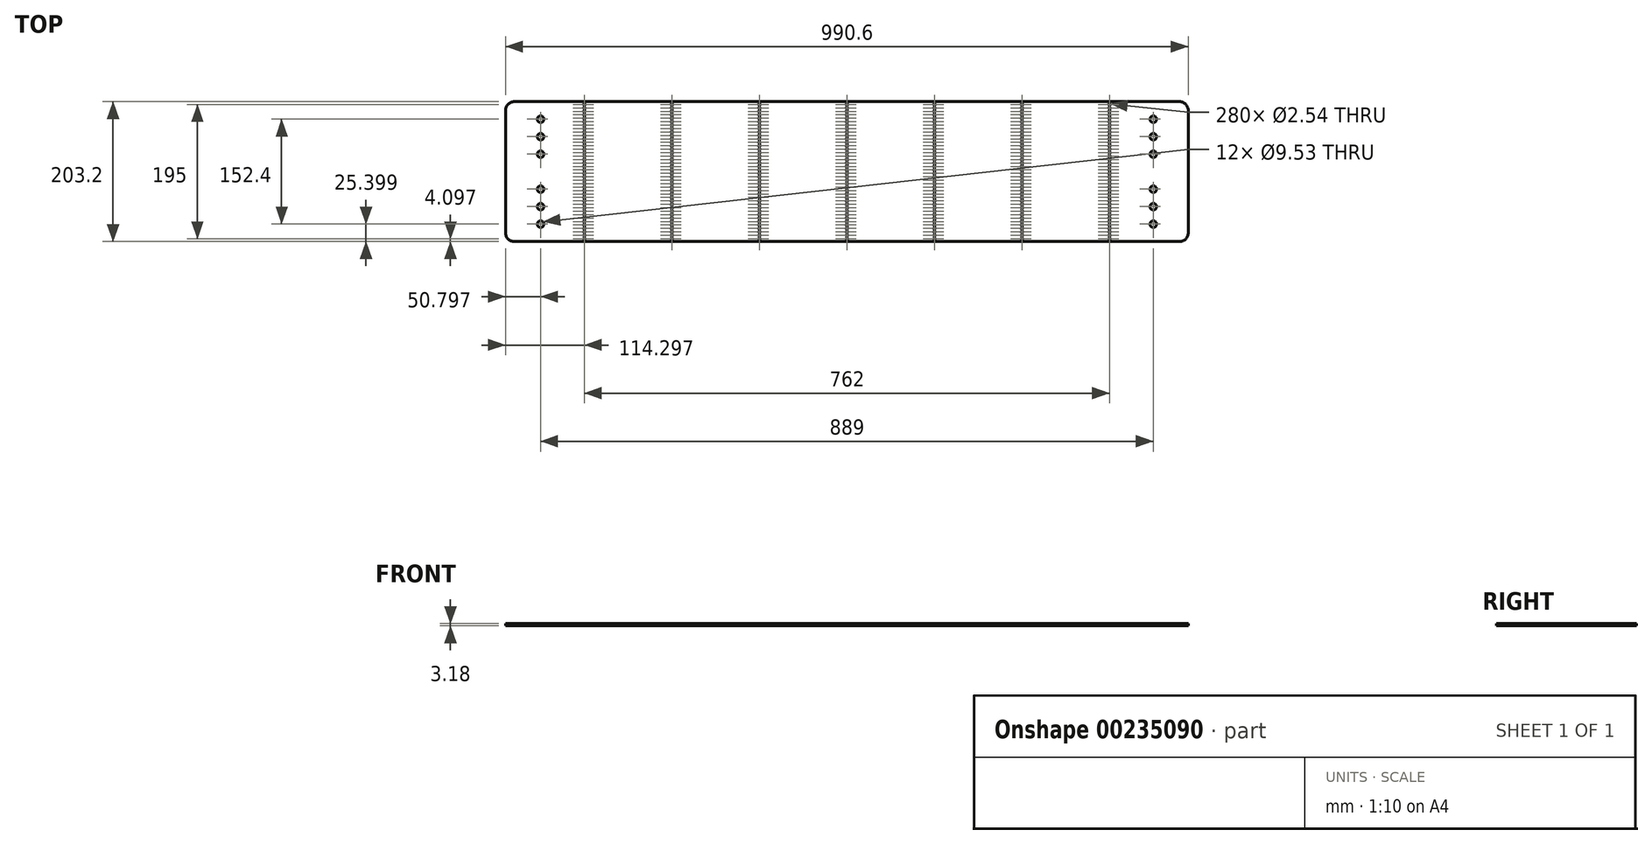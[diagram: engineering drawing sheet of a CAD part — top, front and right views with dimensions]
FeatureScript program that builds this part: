
annotation { "Feature Type Name" : "Feature", "Feature Type Description" : "" }
export const myFeature = defineFeature(function(context is Context, id is Id, definition is map)
    precondition{}
    {
        {
            var Q0;
            Q0=qCreatedBy(makeId("Top.planeOp"),FACE);
            var sketch = newSketch(context, id + "F0", { "sketchPlane" : qUnion([Q0])});
            skLineSegment(sketch, "E0.bottom", {"start": v(-546.73, 39.92) * mm, "end": v(418.47, 39.92) * mm});
            skLineSegment(sketch, "E0.top", {"start": v(-546.73, -163.28) * mm, "end": v(418.47, -163.28) * mm});
            skLineSegment(sketch, "E0.left", {"start": v(-559.43, 27.22) * mm, "end": v(-559.43, -150.58) * mm});
            skLineSegment(sketch, "E0.right", {"start": v(431.17, 27.22) * mm, "end": v(431.17, -150.58) * mm});
            skPoint(sketch, "E1.visualSharp", {"position": v(-559.43, 39.92) * mm});
            skArc(sketch, "E1.filletArc", {"start": v(-546.73, 39.92) * mm, "mid": v(-555.71, 36.2) * mm, "end": v(-559.43, 27.22) * mm});
            skPoint(sketch, "E2.visualSharp", {"position": v(-559.43, -163.28) * mm});
            skArc(sketch, "E2.filletArc", {"start": v(-559.43, -150.58) * mm, "mid": v(-555.71, -159.56) * mm, "end": v(-546.73, -163.28) * mm});
            skArc(sketch, "E3.filletArc", {"start": v(431.17, 27.22) * mm, "mid": v(427.45, 36.2) * mm, "end": v(418.47, 39.92) * mm});
            skArc(sketch, "E4.filletArc", {"start": v(418.47, -163.28) * mm, "mid": v(427.45, -159.56) * mm, "end": v(431.17, -150.58) * mm});
            skLineSegment(sketch, "E5", {"start": v(-559.43, -61.68) * mm, "end": v(-508.63, -61.68) * mm, "construction": true});
            skLineSegment(sketch, "E6", {"start": v(-508.63, 39.92) * mm, "end": v(-508.63, 14.52) * mm, "construction": true});
            skLineSegment(sketch, "E7", {"start": v(-508.63, -61.68) * mm, "end": v(-508.63, -87.08) * mm, "construction": true});
            skLineSegment(sketch, "E8", {"start": v(-508.63, -10.88) * mm, "end": v(-508.63, -36.28) * mm, "construction": true});
            skLineSegment(sketch, "E9", {"start": v(-508.63, -112.48) * mm, "end": v(-508.63, -137.88) * mm, "construction": true});
            skLineSegment(sketch, "E10", {"start": v(-508.63, 14.52) * mm, "end": v(-508.63, -10.88) * mm, "construction": true});
            skLineSegment(sketch, "E11", {"start": v(-508.63, -36.28) * mm, "end": v(-508.63, -61.68) * mm, "construction": true});
            skLineSegment(sketch, "E12", {"start": v(-508.63, -87.08) * mm, "end": v(-508.63, -112.48) * mm, "construction": true});
            skLineSegment(sketch, "E13", {"start": v(-508.63, -137.88) * mm, "end": v(-508.63, -163.28) * mm, "construction": true});
            skCircle(sketch, "E14", {"center": v(-508.63, 14.52) * mm, "radius": 4.76 * mm});
            skCircle(sketch, "E15", {"center": v(-508.63, -10.88) * mm, "radius": 4.76 * mm});
            skCircle(sketch, "E16", {"center": v(-508.63, -36.28) * mm, "radius": 4.76 * mm});
            skCircle(sketch, "E17", {"center": v(-508.63, -87.08) * mm, "radius": 4.76 * mm});
            skCircle(sketch, "E18", {"center": v(-508.63, -112.48) * mm, "radius": 4.76 * mm});
            skCircle(sketch, "E19", {"center": v(-508.63, -137.88) * mm, "radius": 4.76 * mm});
            skLineSegment(sketch, "E20", {"start": v(431.17, -61.68) * mm, "end": v(380.37, -61.68) * mm, "construction": true});
            skLineSegment(sketch, "E21", {"start": v(380.37, 39.92) * mm, "end": v(380.37, -163.28) * mm, "construction": true});
            skCircle(sketch, "E22", {"center": v(380.37, 14.52) * mm, "radius": 4.76 * mm});
            skCircle(sketch, "E23", {"center": v(380.37, -10.88) * mm, "radius": 4.76 * mm});
            skCircle(sketch, "E24", {"center": v(380.37, -36.28) * mm, "radius": 4.76 * mm});
            skCircle(sketch, "E25", {"center": v(380.37, -112.48) * mm, "radius": 4.76 * mm});
            skCircle(sketch, "E26", {"center": v(380.37, -87.08) * mm, "radius": 4.76 * mm});
            skCircle(sketch, "E27", {"center": v(380.37, -137.88) * mm, "radius": 4.76 * mm});
            skLineSegment(sketch, "E28", {"start": v(-508.63, -61.68) * mm, "end": v(-445.13, -61.68) * mm, "construction": true});
            skLineSegment(sketch, "E29", {"start": v(-445.13, 39.92) * mm, "end": v(-445.13, 35.82) * mm});
            skCircle(sketch, "E30", {"center": v(-445.13, 35.82) * mm, "radius": 1.27 * mm});
            skLineSegment(sketch, "E31.direction1", {"start": v(-445.13, 35.82) * mm, "end": v(-445.13, 35.82) * mm});
            skLineSegment(sketch, "E32", {"start": v(-432.43, -159.18) * mm, "end": v(-432.43, -163.28) * mm, "construction": true});
            skCircle(sketch, "E33.0.1.0", {"center": v(-445.13, 30.82) * mm, "radius": 1.27 * mm});
            skCircle(sketch, "E33.1.0.0", {"center": v(-318.13, 35.82) * mm, "radius": 1.27 * mm});
            skCircle(sketch, "E33.1.1.0", {"center": v(-318.13, 30.82) * mm, "radius": 1.27 * mm});
            skCircle(sketch, "E33.2.0.0", {"center": v(-191.13, 35.82) * mm, "radius": 1.27 * mm});
            skCircle(sketch, "E33.2.1.0", {"center": v(-191.13, 30.82) * mm, "radius": 1.27 * mm});
            skLineSegment(sketch, "E33.direction1", {"start": v(-445.13, 35.82) * mm, "end": v(-318.13, 35.82) * mm, "construction": true});
            skLineSegment(sketch, "E33.direction2", {"start": v(-445.13, 35.82) * mm, "end": v(-445.13, 30.82) * mm, "construction": true});
            skCircle(sketch, "E34.0.0.2", {"center": v(-445.13, 25.82) * mm, "radius": 1.27 * mm});
            skCircle(sketch, "E34.0.0.3", {"center": v(-445.13, 20.82) * mm, "radius": 1.27 * mm});
            skCircle(sketch, "E34.0.0.4", {"center": v(-445.13, 15.82) * mm, "radius": 1.27 * mm});
            skCircle(sketch, "E34.0.0.5", {"center": v(-445.13, 10.82) * mm, "radius": 1.27 * mm});
            skCircle(sketch, "E34.0.0.6", {"center": v(-445.13, 5.82) * mm, "radius": 1.27 * mm});
            skCircle(sketch, "E34.0.0.7", {"center": v(-445.13, 0.82) * mm, "radius": 1.27 * mm});
            skCircle(sketch, "E34.0.0.8", {"center": v(-445.13, -4.18) * mm, "radius": 1.27 * mm});
            skCircle(sketch, "E34.0.0.9", {"center": v(-445.13, -9.18) * mm, "radius": 1.27 * mm});
            skCircle(sketch, "E34.0.0.10", {"center": v(-445.13, -14.18) * mm, "radius": 1.27 * mm});
            skCircle(sketch, "E34.0.0.11", {"center": v(-445.13, -19.18) * mm, "radius": 1.27 * mm});
            skCircle(sketch, "E34.0.0.12", {"center": v(-445.13, -24.18) * mm, "radius": 1.27 * mm});
            skCircle(sketch, "E34.0.0.13", {"center": v(-445.13, -29.18) * mm, "radius": 1.27 * mm});
            skCircle(sketch, "E34.0.0.14", {"center": v(-445.13, -34.18) * mm, "radius": 1.27 * mm});
            skCircle(sketch, "E34.0.0.15", {"center": v(-445.13, -39.18) * mm, "radius": 1.27 * mm});
            skCircle(sketch, "E34.0.0.16", {"center": v(-445.13, -44.18) * mm, "radius": 1.27 * mm});
            skCircle(sketch, "E34.0.0.17", {"center": v(-445.13, -49.18) * mm, "radius": 1.27 * mm});
            skCircle(sketch, "E34.0.0.18", {"center": v(-445.13, -54.18) * mm, "radius": 1.27 * mm});
            skCircle(sketch, "E34.0.0.19", {"center": v(-445.13, -59.18) * mm, "radius": 1.27 * mm});
            skCircle(sketch, "E34.0.0.20", {"center": v(-445.13, -64.18) * mm, "radius": 1.27 * mm});
            skCircle(sketch, "E34.0.0.21", {"center": v(-445.13, -69.18) * mm, "radius": 1.27 * mm});
            skCircle(sketch, "E34.0.0.22", {"center": v(-445.13, -74.18) * mm, "radius": 1.27 * mm});
            skCircle(sketch, "E34.0.0.23", {"center": v(-445.13, -79.18) * mm, "radius": 1.27 * mm});
            skCircle(sketch, "E34.0.0.24", {"center": v(-445.13, -84.18) * mm, "radius": 1.27 * mm});
            skCircle(sketch, "E34.0.0.25", {"center": v(-445.13, -89.18) * mm, "radius": 1.27 * mm});
            skCircle(sketch, "E34.0.0.26", {"center": v(-445.13, -94.18) * mm, "radius": 1.27 * mm});
            skCircle(sketch, "E34.0.0.27", {"center": v(-445.13, -99.18) * mm, "radius": 1.27 * mm});
            skCircle(sketch, "E34.0.0.28", {"center": v(-445.13, -104.18) * mm, "radius": 1.27 * mm});
            skCircle(sketch, "E34.0.0.29", {"center": v(-445.13, -109.18) * mm, "radius": 1.27 * mm});
            skCircle(sketch, "E34.0.0.30", {"center": v(-445.13, -114.18) * mm, "radius": 1.27 * mm});
            skCircle(sketch, "E34.0.0.31", {"center": v(-445.13, -119.18) * mm, "radius": 1.27 * mm});
            skCircle(sketch, "E34.0.0.32", {"center": v(-445.13, -124.18) * mm, "radius": 1.27 * mm});
            skCircle(sketch, "E34.0.0.33", {"center": v(-445.13, -129.18) * mm, "radius": 1.27 * mm});
            skCircle(sketch, "E34.0.0.34", {"center": v(-445.13, -134.18) * mm, "radius": 1.27 * mm});
            skCircle(sketch, "E34.0.0.35", {"center": v(-445.13, -139.18) * mm, "radius": 1.27 * mm});
            skCircle(sketch, "E34.0.0.36", {"center": v(-445.13, -144.18) * mm, "radius": 1.27 * mm});
            skCircle(sketch, "E34.0.0.37", {"center": v(-445.13, -149.18) * mm, "radius": 1.27 * mm});
            skCircle(sketch, "E34.0.0.38", {"center": v(-445.13, -154.18) * mm, "radius": 1.27 * mm});
            skCircle(sketch, "E34.0.0.39", {"center": v(-445.13, -159.18) * mm, "radius": 1.27 * mm});
            skCircle(sketch, "E34.0.1.2", {"center": v(-318.13, 25.82) * mm, "radius": 1.27 * mm});
            skCircle(sketch, "E34.0.1.3", {"center": v(-318.13, 20.82) * mm, "radius": 1.27 * mm});
            skCircle(sketch, "E34.0.1.4", {"center": v(-318.13, 15.82) * mm, "radius": 1.27 * mm});
            skCircle(sketch, "E34.0.1.5", {"center": v(-318.13, 10.82) * mm, "radius": 1.27 * mm});
            skCircle(sketch, "E34.0.1.6", {"center": v(-318.13, 5.82) * mm, "radius": 1.27 * mm});
            skCircle(sketch, "E34.0.1.7", {"center": v(-318.13, 0.82) * mm, "radius": 1.27 * mm});
            skCircle(sketch, "E34.0.1.8", {"center": v(-318.13, -4.18) * mm, "radius": 1.27 * mm});
            skCircle(sketch, "E34.0.1.9", {"center": v(-318.13, -9.18) * mm, "radius": 1.27 * mm});
            skCircle(sketch, "E34.0.1.10", {"center": v(-318.13, -14.18) * mm, "radius": 1.27 * mm});
            skCircle(sketch, "E34.0.1.11", {"center": v(-318.13, -19.18) * mm, "radius": 1.27 * mm});
            skCircle(sketch, "E34.0.1.12", {"center": v(-318.13, -24.18) * mm, "radius": 1.27 * mm});
            skCircle(sketch, "E34.0.1.13", {"center": v(-318.13, -29.18) * mm, "radius": 1.27 * mm});
            skCircle(sketch, "E34.0.1.14", {"center": v(-318.13, -34.18) * mm, "radius": 1.27 * mm});
            skCircle(sketch, "E34.0.1.15", {"center": v(-318.13, -39.18) * mm, "radius": 1.27 * mm});
            skCircle(sketch, "E34.0.1.16", {"center": v(-318.13, -44.18) * mm, "radius": 1.27 * mm});
            skCircle(sketch, "E34.0.1.17", {"center": v(-318.13, -49.18) * mm, "radius": 1.27 * mm});
            skCircle(sketch, "E34.0.1.18", {"center": v(-318.13, -54.18) * mm, "radius": 1.27 * mm});
            skCircle(sketch, "E34.0.1.19", {"center": v(-318.13, -59.18) * mm, "radius": 1.27 * mm});
            skCircle(sketch, "E34.0.1.20", {"center": v(-318.13, -64.18) * mm, "radius": 1.27 * mm});
            skCircle(sketch, "E34.0.1.21", {"center": v(-318.13, -69.18) * mm, "radius": 1.27 * mm});
            skCircle(sketch, "E34.0.1.22", {"center": v(-318.13, -74.18) * mm, "radius": 1.27 * mm});
            skCircle(sketch, "E34.0.1.23", {"center": v(-318.13, -79.18) * mm, "radius": 1.27 * mm});
            skCircle(sketch, "E34.0.1.24", {"center": v(-318.13, -84.18) * mm, "radius": 1.27 * mm});
            skCircle(sketch, "E34.0.1.25", {"center": v(-318.13, -89.18) * mm, "radius": 1.27 * mm});
            skCircle(sketch, "E34.0.1.26", {"center": v(-318.13, -94.18) * mm, "radius": 1.27 * mm});
            skCircle(sketch, "E34.0.1.27", {"center": v(-318.13, -99.18) * mm, "radius": 1.27 * mm});
            skCircle(sketch, "E34.0.1.28", {"center": v(-318.13, -104.18) * mm, "radius": 1.27 * mm});
            skCircle(sketch, "E34.0.1.29", {"center": v(-318.13, -109.18) * mm, "radius": 1.27 * mm});
            skCircle(sketch, "E34.0.1.30", {"center": v(-318.13, -114.18) * mm, "radius": 1.27 * mm});
            skCircle(sketch, "E34.0.1.31", {"center": v(-318.13, -119.18) * mm, "radius": 1.27 * mm});
            skCircle(sketch, "E34.0.1.32", {"center": v(-318.13, -124.18) * mm, "radius": 1.27 * mm});
            skCircle(sketch, "E34.0.1.33", {"center": v(-318.13, -129.18) * mm, "radius": 1.27 * mm});
            skCircle(sketch, "E34.0.1.34", {"center": v(-318.13, -134.18) * mm, "radius": 1.27 * mm});
            skCircle(sketch, "E34.0.1.35", {"center": v(-318.13, -139.18) * mm, "radius": 1.27 * mm});
            skCircle(sketch, "E34.0.1.36", {"center": v(-318.13, -144.18) * mm, "radius": 1.27 * mm});
            skCircle(sketch, "E34.0.1.37", {"center": v(-318.13, -149.18) * mm, "radius": 1.27 * mm});
            skCircle(sketch, "E34.0.1.38", {"center": v(-318.13, -154.18) * mm, "radius": 1.27 * mm});
            skCircle(sketch, "E34.0.1.39", {"center": v(-318.13, -159.18) * mm, "radius": 1.27 * mm});
            skCircle(sketch, "E34.0.2.2", {"center": v(-191.13, 25.82) * mm, "radius": 1.27 * mm});
            skCircle(sketch, "E34.0.2.3", {"center": v(-191.13, 20.82) * mm, "radius": 1.27 * mm});
            skCircle(sketch, "E34.0.2.4", {"center": v(-191.13, 15.82) * mm, "radius": 1.27 * mm});
            skCircle(sketch, "E34.0.2.5", {"center": v(-191.13, 10.82) * mm, "radius": 1.27 * mm});
            skCircle(sketch, "E34.0.2.6", {"center": v(-191.13, 5.82) * mm, "radius": 1.27 * mm});
            skCircle(sketch, "E34.0.2.7", {"center": v(-191.13, 0.82) * mm, "radius": 1.27 * mm});
            skCircle(sketch, "E34.0.2.8", {"center": v(-191.13, -4.18) * mm, "radius": 1.27 * mm});
            skCircle(sketch, "E34.0.2.9", {"center": v(-191.13, -9.18) * mm, "radius": 1.27 * mm});
            skCircle(sketch, "E34.0.2.10", {"center": v(-191.13, -14.18) * mm, "radius": 1.27 * mm});
            skCircle(sketch, "E34.0.2.11", {"center": v(-191.13, -19.18) * mm, "radius": 1.27 * mm});
            skCircle(sketch, "E34.0.2.12", {"center": v(-191.13, -24.18) * mm, "radius": 1.27 * mm});
            skCircle(sketch, "E34.0.2.13", {"center": v(-191.13, -29.18) * mm, "radius": 1.27 * mm});
            skCircle(sketch, "E34.0.2.14", {"center": v(-191.13, -34.18) * mm, "radius": 1.27 * mm});
            skCircle(sketch, "E34.0.2.15", {"center": v(-191.13, -39.18) * mm, "radius": 1.27 * mm});
            skCircle(sketch, "E34.0.2.16", {"center": v(-191.13, -44.18) * mm, "radius": 1.27 * mm});
            skCircle(sketch, "E34.0.2.17", {"center": v(-191.13, -49.18) * mm, "radius": 1.27 * mm});
            skCircle(sketch, "E34.0.2.18", {"center": v(-191.13, -54.18) * mm, "radius": 1.27 * mm});
            skCircle(sketch, "E34.0.2.19", {"center": v(-191.13, -59.18) * mm, "radius": 1.27 * mm});
            skCircle(sketch, "E34.0.2.20", {"center": v(-191.13, -64.18) * mm, "radius": 1.27 * mm});
            skCircle(sketch, "E34.0.2.21", {"center": v(-191.13, -69.18) * mm, "radius": 1.27 * mm});
            skCircle(sketch, "E34.0.2.22", {"center": v(-191.13, -74.18) * mm, "radius": 1.27 * mm});
            skCircle(sketch, "E34.0.2.23", {"center": v(-191.13, -79.18) * mm, "radius": 1.27 * mm});
            skCircle(sketch, "E34.0.2.24", {"center": v(-191.13, -84.18) * mm, "radius": 1.27 * mm});
            skCircle(sketch, "E34.0.2.25", {"center": v(-191.13, -89.18) * mm, "radius": 1.27 * mm});
            skCircle(sketch, "E34.0.2.26", {"center": v(-191.13, -94.18) * mm, "radius": 1.27 * mm});
            skCircle(sketch, "E34.0.2.27", {"center": v(-191.13, -99.18) * mm, "radius": 1.27 * mm});
            skCircle(sketch, "E34.0.2.28", {"center": v(-191.13, -104.18) * mm, "radius": 1.27 * mm});
            skCircle(sketch, "E34.0.2.29", {"center": v(-191.13, -109.18) * mm, "radius": 1.27 * mm});
            skCircle(sketch, "E34.0.2.30", {"center": v(-191.13, -114.18) * mm, "radius": 1.27 * mm});
            skCircle(sketch, "E34.0.2.31", {"center": v(-191.13, -119.18) * mm, "radius": 1.27 * mm});
            skCircle(sketch, "E34.0.2.32", {"center": v(-191.13, -124.18) * mm, "radius": 1.27 * mm});
            skCircle(sketch, "E34.0.2.33", {"center": v(-191.13, -129.18) * mm, "radius": 1.27 * mm});
            skCircle(sketch, "E34.0.2.34", {"center": v(-191.13, -134.18) * mm, "radius": 1.27 * mm});
            skCircle(sketch, "E34.0.2.35", {"center": v(-191.13, -139.18) * mm, "radius": 1.27 * mm});
            skCircle(sketch, "E34.0.2.36", {"center": v(-191.13, -144.18) * mm, "radius": 1.27 * mm});
            skCircle(sketch, "E34.0.2.37", {"center": v(-191.13, -149.18) * mm, "radius": 1.27 * mm});
            skCircle(sketch, "E34.0.2.38", {"center": v(-191.13, -154.18) * mm, "radius": 1.27 * mm});
            skCircle(sketch, "E34.0.2.39", {"center": v(-191.13, -159.18) * mm, "radius": 1.27 * mm});
            skCircle(sketch, "E35.0.3.0", {"center": v(-64.13, 35.82) * mm, "radius": 1.27 * mm});
            skCircle(sketch, "E35.0.3.1", {"center": v(-64.13, 30.82) * mm, "radius": 1.27 * mm});
            skCircle(sketch, "E35.0.3.2", {"center": v(-64.13, 25.82) * mm, "radius": 1.27 * mm});
            skCircle(sketch, "E35.0.3.3", {"center": v(-64.13, 20.82) * mm, "radius": 1.27 * mm});
            skCircle(sketch, "E35.0.3.4", {"center": v(-64.13, 15.82) * mm, "radius": 1.27 * mm});
            skCircle(sketch, "E35.0.3.5", {"center": v(-64.13, 10.82) * mm, "radius": 1.27 * mm});
            skCircle(sketch, "E35.0.3.6", {"center": v(-64.13, 5.82) * mm, "radius": 1.27 * mm});
            skCircle(sketch, "E35.0.3.7", {"center": v(-64.13, 0.82) * mm, "radius": 1.27 * mm});
            skCircle(sketch, "E35.0.3.8", {"center": v(-64.13, -4.18) * mm, "radius": 1.27 * mm});
            skCircle(sketch, "E35.0.3.9", {"center": v(-64.13, -9.18) * mm, "radius": 1.27 * mm});
            skCircle(sketch, "E35.0.3.10", {"center": v(-64.13, -14.18) * mm, "radius": 1.27 * mm});
            skCircle(sketch, "E35.0.3.11", {"center": v(-64.13, -19.18) * mm, "radius": 1.27 * mm});
            skCircle(sketch, "E35.0.3.12", {"center": v(-64.13, -24.18) * mm, "radius": 1.27 * mm});
            skCircle(sketch, "E35.0.3.13", {"center": v(-64.13, -29.18) * mm, "radius": 1.27 * mm});
            skCircle(sketch, "E35.0.3.14", {"center": v(-64.13, -34.18) * mm, "radius": 1.27 * mm});
            skCircle(sketch, "E35.0.3.15", {"center": v(-64.13, -39.18) * mm, "radius": 1.27 * mm});
            skCircle(sketch, "E35.0.3.16", {"center": v(-64.13, -44.18) * mm, "radius": 1.27 * mm});
            skCircle(sketch, "E35.0.3.17", {"center": v(-64.13, -49.18) * mm, "radius": 1.27 * mm});
            skCircle(sketch, "E35.0.3.18", {"center": v(-64.13, -54.18) * mm, "radius": 1.27 * mm});
            skCircle(sketch, "E35.0.3.19", {"center": v(-64.13, -59.18) * mm, "radius": 1.27 * mm});
            skCircle(sketch, "E35.0.3.20", {"center": v(-64.13, -64.18) * mm, "radius": 1.27 * mm});
            skCircle(sketch, "E35.0.3.21", {"center": v(-64.13, -69.18) * mm, "radius": 1.27 * mm});
            skCircle(sketch, "E35.0.3.22", {"center": v(-64.13, -74.18) * mm, "radius": 1.27 * mm});
            skCircle(sketch, "E35.0.3.23", {"center": v(-64.13, -79.18) * mm, "radius": 1.27 * mm});
            skCircle(sketch, "E35.0.3.24", {"center": v(-64.13, -84.18) * mm, "radius": 1.27 * mm});
            skCircle(sketch, "E35.0.3.25", {"center": v(-64.13, -89.18) * mm, "radius": 1.27 * mm});
            skCircle(sketch, "E35.0.3.26", {"center": v(-64.13, -94.18) * mm, "radius": 1.27 * mm});
            skCircle(sketch, "E35.0.3.27", {"center": v(-64.13, -99.18) * mm, "radius": 1.27 * mm});
            skCircle(sketch, "E35.0.3.28", {"center": v(-64.13, -104.18) * mm, "radius": 1.27 * mm});
            skCircle(sketch, "E35.0.3.29", {"center": v(-64.13, -109.18) * mm, "radius": 1.27 * mm});
            skCircle(sketch, "E35.0.3.30", {"center": v(-64.13, -114.18) * mm, "radius": 1.27 * mm});
            skCircle(sketch, "E35.0.3.31", {"center": v(-64.13, -119.18) * mm, "radius": 1.27 * mm});
            skCircle(sketch, "E35.0.3.32", {"center": v(-64.13, -124.18) * mm, "radius": 1.27 * mm});
            skCircle(sketch, "E35.0.3.33", {"center": v(-64.13, -129.18) * mm, "radius": 1.27 * mm});
            skCircle(sketch, "E35.0.3.34", {"center": v(-64.13, -134.18) * mm, "radius": 1.27 * mm});
            skCircle(sketch, "E35.0.3.35", {"center": v(-64.13, -139.18) * mm, "radius": 1.27 * mm});
            skCircle(sketch, "E35.0.3.36", {"center": v(-64.13, -144.18) * mm, "radius": 1.27 * mm});
            skCircle(sketch, "E35.0.3.37", {"center": v(-64.13, -149.18) * mm, "radius": 1.27 * mm});
            skCircle(sketch, "E35.0.3.38", {"center": v(-64.13, -154.18) * mm, "radius": 1.27 * mm});
            skCircle(sketch, "E35.0.3.39", {"center": v(-64.13, -159.18) * mm, "radius": 1.27 * mm});
            skCircle(sketch, "E35.0.4.0", {"center": v(62.87, 35.82) * mm, "radius": 1.27 * mm});
            skCircle(sketch, "E35.0.4.1", {"center": v(62.87, 30.82) * mm, "radius": 1.27 * mm});
            skCircle(sketch, "E35.0.4.2", {"center": v(62.87, 25.82) * mm, "radius": 1.27 * mm});
            skCircle(sketch, "E35.0.4.3", {"center": v(62.87, 20.82) * mm, "radius": 1.27 * mm});
            skCircle(sketch, "E35.0.4.4", {"center": v(62.87, 15.82) * mm, "radius": 1.27 * mm});
            skCircle(sketch, "E35.0.4.5", {"center": v(62.87, 10.82) * mm, "radius": 1.27 * mm});
            skCircle(sketch, "E35.0.4.6", {"center": v(62.87, 5.82) * mm, "radius": 1.27 * mm});
            skCircle(sketch, "E35.0.4.7", {"center": v(62.87, 0.82) * mm, "radius": 1.27 * mm});
            skCircle(sketch, "E35.0.4.8", {"center": v(62.87, -4.18) * mm, "radius": 1.27 * mm});
            skCircle(sketch, "E35.0.4.9", {"center": v(62.87, -9.18) * mm, "radius": 1.27 * mm});
            skCircle(sketch, "E35.0.4.10", {"center": v(62.87, -14.18) * mm, "radius": 1.27 * mm});
            skCircle(sketch, "E35.0.4.11", {"center": v(62.87, -19.18) * mm, "radius": 1.27 * mm});
            skCircle(sketch, "E35.0.4.12", {"center": v(62.87, -24.18) * mm, "radius": 1.27 * mm});
            skCircle(sketch, "E35.0.4.13", {"center": v(62.87, -29.18) * mm, "radius": 1.27 * mm});
            skCircle(sketch, "E35.0.4.14", {"center": v(62.87, -34.18) * mm, "radius": 1.27 * mm});
            skCircle(sketch, "E35.0.4.15", {"center": v(62.87, -39.18) * mm, "radius": 1.27 * mm});
            skCircle(sketch, "E35.0.4.16", {"center": v(62.87, -44.18) * mm, "radius": 1.27 * mm});
            skCircle(sketch, "E35.0.4.17", {"center": v(62.87, -49.18) * mm, "radius": 1.27 * mm});
            skCircle(sketch, "E35.0.4.18", {"center": v(62.87, -54.18) * mm, "radius": 1.27 * mm});
            skCircle(sketch, "E35.0.4.19", {"center": v(62.87, -59.18) * mm, "radius": 1.27 * mm});
            skCircle(sketch, "E35.0.4.20", {"center": v(62.87, -64.18) * mm, "radius": 1.27 * mm});
            skCircle(sketch, "E35.0.4.21", {"center": v(62.87, -69.18) * mm, "radius": 1.27 * mm});
            skCircle(sketch, "E35.0.4.22", {"center": v(62.87, -74.18) * mm, "radius": 1.27 * mm});
            skCircle(sketch, "E35.0.4.23", {"center": v(62.87, -79.18) * mm, "radius": 1.27 * mm});
            skCircle(sketch, "E35.0.4.24", {"center": v(62.87, -84.18) * mm, "radius": 1.27 * mm});
            skCircle(sketch, "E35.0.4.25", {"center": v(62.87, -89.18) * mm, "radius": 1.27 * mm});
            skCircle(sketch, "E35.0.4.26", {"center": v(62.87, -94.18) * mm, "radius": 1.27 * mm});
            skCircle(sketch, "E35.0.4.27", {"center": v(62.87, -99.18) * mm, "radius": 1.27 * mm});
            skCircle(sketch, "E35.0.4.28", {"center": v(62.87, -104.18) * mm, "radius": 1.27 * mm});
            skCircle(sketch, "E35.0.4.29", {"center": v(62.87, -109.18) * mm, "radius": 1.27 * mm});
            skCircle(sketch, "E35.0.4.30", {"center": v(62.87, -114.18) * mm, "radius": 1.27 * mm});
            skCircle(sketch, "E35.0.4.31", {"center": v(62.87, -119.18) * mm, "radius": 1.27 * mm});
            skCircle(sketch, "E35.0.4.32", {"center": v(62.87, -124.18) * mm, "radius": 1.27 * mm});
            skCircle(sketch, "E35.0.4.33", {"center": v(62.87, -129.18) * mm, "radius": 1.27 * mm});
            skCircle(sketch, "E35.0.4.34", {"center": v(62.87, -134.18) * mm, "radius": 1.27 * mm});
            skCircle(sketch, "E35.0.4.35", {"center": v(62.87, -139.18) * mm, "radius": 1.27 * mm});
            skCircle(sketch, "E35.0.4.36", {"center": v(62.87, -144.18) * mm, "radius": 1.27 * mm});
            skCircle(sketch, "E35.0.4.37", {"center": v(62.87, -149.18) * mm, "radius": 1.27 * mm});
            skCircle(sketch, "E35.0.4.38", {"center": v(62.87, -154.18) * mm, "radius": 1.27 * mm});
            skCircle(sketch, "E35.0.4.39", {"center": v(62.87, -159.18) * mm, "radius": 1.27 * mm});
            skCircle(sketch, "E35.0.5.0", {"center": v(189.87, 35.82) * mm, "radius": 1.27 * mm});
            skCircle(sketch, "E35.0.5.1", {"center": v(189.87, 30.82) * mm, "radius": 1.27 * mm});
            skCircle(sketch, "E35.0.5.2", {"center": v(189.87, 25.82) * mm, "radius": 1.27 * mm});
            skCircle(sketch, "E35.0.5.3", {"center": v(189.87, 20.82) * mm, "radius": 1.27 * mm});
            skCircle(sketch, "E35.0.5.4", {"center": v(189.87, 15.82) * mm, "radius": 1.27 * mm});
            skCircle(sketch, "E35.0.5.5", {"center": v(189.87, 10.82) * mm, "radius": 1.27 * mm});
            skCircle(sketch, "E35.0.5.6", {"center": v(189.87, 5.82) * mm, "radius": 1.27 * mm});
            skCircle(sketch, "E35.0.5.7", {"center": v(189.87, 0.82) * mm, "radius": 1.27 * mm});
            skCircle(sketch, "E35.0.5.8", {"center": v(189.87, -4.18) * mm, "radius": 1.27 * mm});
            skCircle(sketch, "E35.0.5.9", {"center": v(189.87, -9.18) * mm, "radius": 1.27 * mm});
            skCircle(sketch, "E35.0.5.10", {"center": v(189.87, -14.18) * mm, "radius": 1.27 * mm});
            skCircle(sketch, "E35.0.5.11", {"center": v(189.87, -19.18) * mm, "radius": 1.27 * mm});
            skCircle(sketch, "E35.0.5.12", {"center": v(189.87, -24.18) * mm, "radius": 1.27 * mm});
            skCircle(sketch, "E35.0.5.13", {"center": v(189.87, -29.18) * mm, "radius": 1.27 * mm});
            skCircle(sketch, "E35.0.5.14", {"center": v(189.87, -34.18) * mm, "radius": 1.27 * mm});
            skCircle(sketch, "E35.0.5.15", {"center": v(189.87, -39.18) * mm, "radius": 1.27 * mm});
            skCircle(sketch, "E35.0.5.16", {"center": v(189.87, -44.18) * mm, "radius": 1.27 * mm});
            skCircle(sketch, "E35.0.5.17", {"center": v(189.87, -49.18) * mm, "radius": 1.27 * mm});
            skCircle(sketch, "E35.0.5.18", {"center": v(189.87, -54.18) * mm, "radius": 1.27 * mm});
            skCircle(sketch, "E35.0.5.19", {"center": v(189.87, -59.18) * mm, "radius": 1.27 * mm});
            skCircle(sketch, "E35.0.5.20", {"center": v(189.87, -64.18) * mm, "radius": 1.27 * mm});
            skCircle(sketch, "E35.0.5.21", {"center": v(189.87, -69.18) * mm, "radius": 1.27 * mm});
            skCircle(sketch, "E35.0.5.22", {"center": v(189.87, -74.18) * mm, "radius": 1.27 * mm});
            skCircle(sketch, "E35.0.5.23", {"center": v(189.87, -79.18) * mm, "radius": 1.27 * mm});
            skCircle(sketch, "E35.0.5.24", {"center": v(189.87, -84.18) * mm, "radius": 1.27 * mm});
            skCircle(sketch, "E35.0.5.25", {"center": v(189.87, -89.18) * mm, "radius": 1.27 * mm});
            skCircle(sketch, "E35.0.5.26", {"center": v(189.87, -94.18) * mm, "radius": 1.27 * mm});
            skCircle(sketch, "E35.0.5.27", {"center": v(189.87, -99.18) * mm, "radius": 1.27 * mm});
            skCircle(sketch, "E35.0.5.28", {"center": v(189.87, -104.18) * mm, "radius": 1.27 * mm});
            skCircle(sketch, "E35.0.5.29", {"center": v(189.87, -109.18) * mm, "radius": 1.27 * mm});
            skCircle(sketch, "E35.0.5.30", {"center": v(189.87, -114.18) * mm, "radius": 1.27 * mm});
            skCircle(sketch, "E35.0.5.31", {"center": v(189.87, -119.18) * mm, "radius": 1.27 * mm});
            skCircle(sketch, "E35.0.5.32", {"center": v(189.87, -124.18) * mm, "radius": 1.27 * mm});
            skCircle(sketch, "E35.0.5.33", {"center": v(189.87, -129.18) * mm, "radius": 1.27 * mm});
            skCircle(sketch, "E35.0.5.34", {"center": v(189.87, -134.18) * mm, "radius": 1.27 * mm});
            skCircle(sketch, "E35.0.5.35", {"center": v(189.87, -139.18) * mm, "radius": 1.27 * mm});
            skCircle(sketch, "E35.0.5.36", {"center": v(189.87, -144.18) * mm, "radius": 1.27 * mm});
            skCircle(sketch, "E35.0.5.37", {"center": v(189.87, -149.18) * mm, "radius": 1.27 * mm});
            skCircle(sketch, "E35.0.5.38", {"center": v(189.87, -154.18) * mm, "radius": 1.27 * mm});
            skCircle(sketch, "E35.0.5.39", {"center": v(189.87, -159.18) * mm, "radius": 1.27 * mm});
            skCircle(sketch, "E35.0.6.0", {"center": v(316.87, 35.82) * mm, "radius": 1.27 * mm});
            skCircle(sketch, "E35.0.6.1", {"center": v(316.87, 30.82) * mm, "radius": 1.27 * mm});
            skCircle(sketch, "E35.0.6.2", {"center": v(316.87, 25.82) * mm, "radius": 1.27 * mm});
            skCircle(sketch, "E35.0.6.3", {"center": v(316.87, 20.82) * mm, "radius": 1.27 * mm});
            skCircle(sketch, "E35.0.6.4", {"center": v(316.87, 15.82) * mm, "radius": 1.27 * mm});
            skCircle(sketch, "E35.0.6.5", {"center": v(316.87, 10.82) * mm, "radius": 1.27 * mm});
            skCircle(sketch, "E35.0.6.6", {"center": v(316.87, 5.82) * mm, "radius": 1.27 * mm});
            skCircle(sketch, "E35.0.6.7", {"center": v(316.87, 0.82) * mm, "radius": 1.27 * mm});
            skCircle(sketch, "E35.0.6.8", {"center": v(316.87, -4.18) * mm, "radius": 1.27 * mm});
            skCircle(sketch, "E35.0.6.9", {"center": v(316.87, -9.18) * mm, "radius": 1.27 * mm});
            skCircle(sketch, "E35.0.6.10", {"center": v(316.87, -14.18) * mm, "radius": 1.27 * mm});
            skCircle(sketch, "E35.0.6.11", {"center": v(316.87, -19.18) * mm, "radius": 1.27 * mm});
            skCircle(sketch, "E35.0.6.12", {"center": v(316.87, -24.18) * mm, "radius": 1.27 * mm});
            skCircle(sketch, "E35.0.6.13", {"center": v(316.87, -29.18) * mm, "radius": 1.27 * mm});
            skCircle(sketch, "E35.0.6.14", {"center": v(316.87, -34.18) * mm, "radius": 1.27 * mm});
            skCircle(sketch, "E35.0.6.15", {"center": v(316.87, -39.18) * mm, "radius": 1.27 * mm});
            skCircle(sketch, "E35.0.6.16", {"center": v(316.87, -44.18) * mm, "radius": 1.27 * mm});
            skCircle(sketch, "E35.0.6.17", {"center": v(316.87, -49.18) * mm, "radius": 1.27 * mm});
            skCircle(sketch, "E35.0.6.18", {"center": v(316.87, -54.18) * mm, "radius": 1.27 * mm});
            skCircle(sketch, "E35.0.6.19", {"center": v(316.87, -59.18) * mm, "radius": 1.27 * mm});
            skCircle(sketch, "E35.0.6.20", {"center": v(316.87, -64.18) * mm, "radius": 1.27 * mm});
            skCircle(sketch, "E35.0.6.21", {"center": v(316.87, -69.18) * mm, "radius": 1.27 * mm});
            skCircle(sketch, "E35.0.6.22", {"center": v(316.87, -74.18) * mm, "radius": 1.27 * mm});
            skCircle(sketch, "E35.0.6.23", {"center": v(316.87, -79.18) * mm, "radius": 1.27 * mm});
            skCircle(sketch, "E35.0.6.24", {"center": v(316.87, -84.18) * mm, "radius": 1.27 * mm});
            skCircle(sketch, "E35.0.6.25", {"center": v(316.87, -89.18) * mm, "radius": 1.27 * mm});
            skCircle(sketch, "E35.0.6.26", {"center": v(316.87, -94.18) * mm, "radius": 1.27 * mm});
            skCircle(sketch, "E35.0.6.27", {"center": v(316.87, -99.18) * mm, "radius": 1.27 * mm});
            skCircle(sketch, "E35.0.6.28", {"center": v(316.87, -104.18) * mm, "radius": 1.27 * mm});
            skCircle(sketch, "E35.0.6.29", {"center": v(316.87, -109.18) * mm, "radius": 1.27 * mm});
            skCircle(sketch, "E35.0.6.30", {"center": v(316.87, -114.18) * mm, "radius": 1.27 * mm});
            skCircle(sketch, "E35.0.6.31", {"center": v(316.87, -119.18) * mm, "radius": 1.27 * mm});
            skCircle(sketch, "E35.0.6.32", {"center": v(316.87, -124.18) * mm, "radius": 1.27 * mm});
            skCircle(sketch, "E35.0.6.33", {"center": v(316.87, -129.18) * mm, "radius": 1.27 * mm});
            skCircle(sketch, "E35.0.6.34", {"center": v(316.87, -134.18) * mm, "radius": 1.27 * mm});
            skCircle(sketch, "E35.0.6.35", {"center": v(316.87, -139.18) * mm, "radius": 1.27 * mm});
            skCircle(sketch, "E35.0.6.36", {"center": v(316.87, -144.18) * mm, "radius": 1.27 * mm});
            skCircle(sketch, "E35.0.6.37", {"center": v(316.87, -149.18) * mm, "radius": 1.27 * mm});
            skCircle(sketch, "E35.0.6.38", {"center": v(316.87, -154.18) * mm, "radius": 1.27 * mm});
            skCircle(sketch, "E35.0.6.39", {"center": v(316.87, -159.18) * mm, "radius": 1.27 * mm});
            skSolve(sketch);
        }
        {
            var Q0;
            Q0 = qSketchRegion(id + "F0", true);
            extrude(context, id + "F1", {"entities" : qUnion([Q0]), "depth" : 3.17 * mm});
        }
    });
